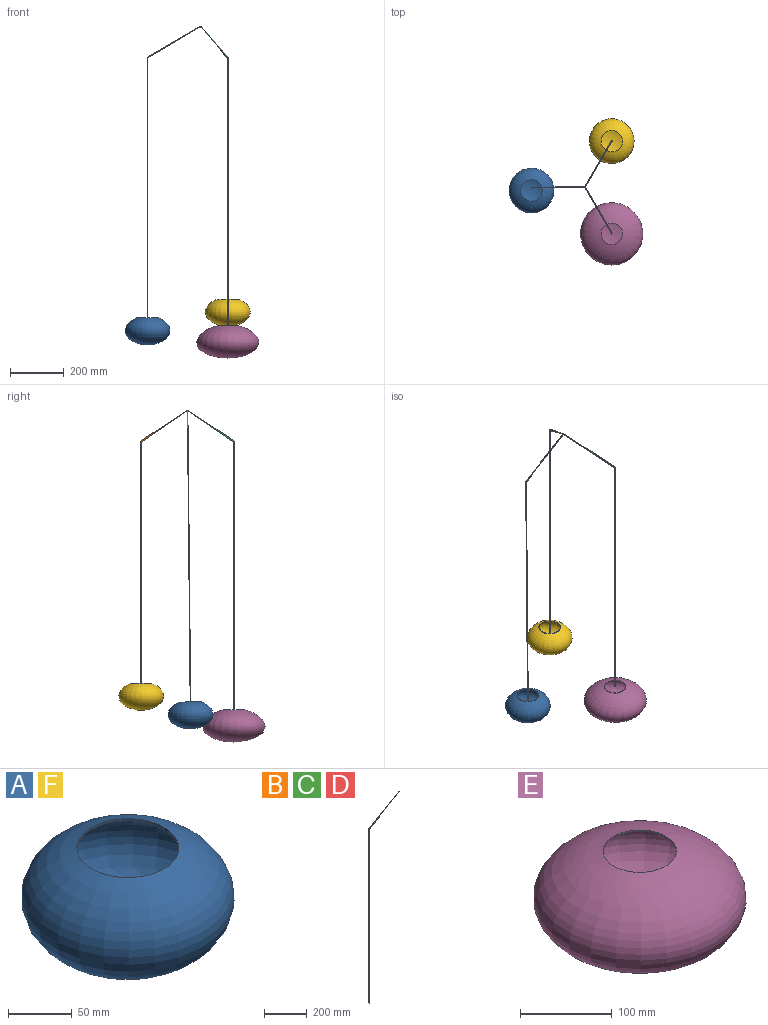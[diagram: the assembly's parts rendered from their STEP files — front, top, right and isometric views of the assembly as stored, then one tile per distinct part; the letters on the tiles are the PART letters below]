
ASSEMBLY  parts=6 mates=3
PART A: 3 faces, bbox 166.8x166.8x100 mm
  f0: revolved ~166.78x166.78mm, area 62131mm2, adj f1
  f1: cylinder r=40mm len=80mm, axis (0,0,1), area 502.7mm2, adj f0,f2
  f2: revolved ~164.07x164.07mm, area 59317.3mm2, adj f1
PART B: 8 faces, bbox 200x2x1115.5 mm
  f0: plane 1000x2mm, normal (-1,0,0), area 2000mm2, adj f1,f5,f6,f7
  f1: plane 2x2mm, normal (0,0,-1), area 4mm2, adj f0,f2,f6,f7
  f2: plane 995.79x2mm, normal (1,0,0), area 1991.6mm2, adj f1,f3,f6,f7
  f3: plane 198x117.68mm, normal (0.51,0,-0.86), area 460.7mm2, adj f2,f4,f6,f7
  f4: plane 2x2mm, normal (1,0,0), area 4mm2, adj f3,f5,f6,f7
  f5: plane 200x115.47mm, normal (-0.5,0,0.87), area 461.9mm2, adj f0,f4,f6,f7
  f6: plane 1115.47x200mm, normal (0,-1,0), area 2730.7mm2, adj f0,f1,f2,f3,f4,f5
  f7: plane 1115.47x200mm, normal (0,1,0), area 2730.7mm2, adj f0,f1,f2,f3,f4,f5
PART C: same geometry as B
PART D: same geometry as B
PART E: 3 faces, bbox 232.2x232.2x120 mm
  f0: revolved ~232.21x232.21mm, area 114546.4mm2, adj f1
  f1: cylinder r=40mm len=80mm, axis (0,0,1), area 502.7mm2, adj f0,f2
  f2: revolved ~227.84x227.84mm, area 109548.3mm2, adj f1
PART F: same geometry as A
PLACE A rot(axis=(-0.97,-0.01,0.26),0.6deg) t=(401.09,-9.72,-1135.4)mm
PLACE B rot(axis=(0,0,-1),120deg) t=(-450.53,-782.34,-1114.47)mm
PLACE C rot(axis=(0,0,1),120deg) t=(-452.26,781.34,-1114.47)mm
PLACE D rot(axis=(-0.97,-0.01,0.26),0.6deg) t=(902.88,-7.24,-1114.38)mm
PLACE E rot(axis=(0,0,1),30deg) t=(-420.12,-472.34,-1174.47)mm
PLACE F rot(axis=(0,0,-1),30deg) t=(619.12,-127.66,-1066.47)mm
MATE slider E.f1 <-> C.f1  axis (0,0,1) through (99.5,-172.34,-1114.47)mm
MATE slider F.f1 <-> B.f1  axis (0,0,1) through (99.5,172.34,-1016.47)mm
MATE slider A.f1 <-> D.f1  axis (0,0.01,1) through (-198.91,-10.77,-1085.43)mm
